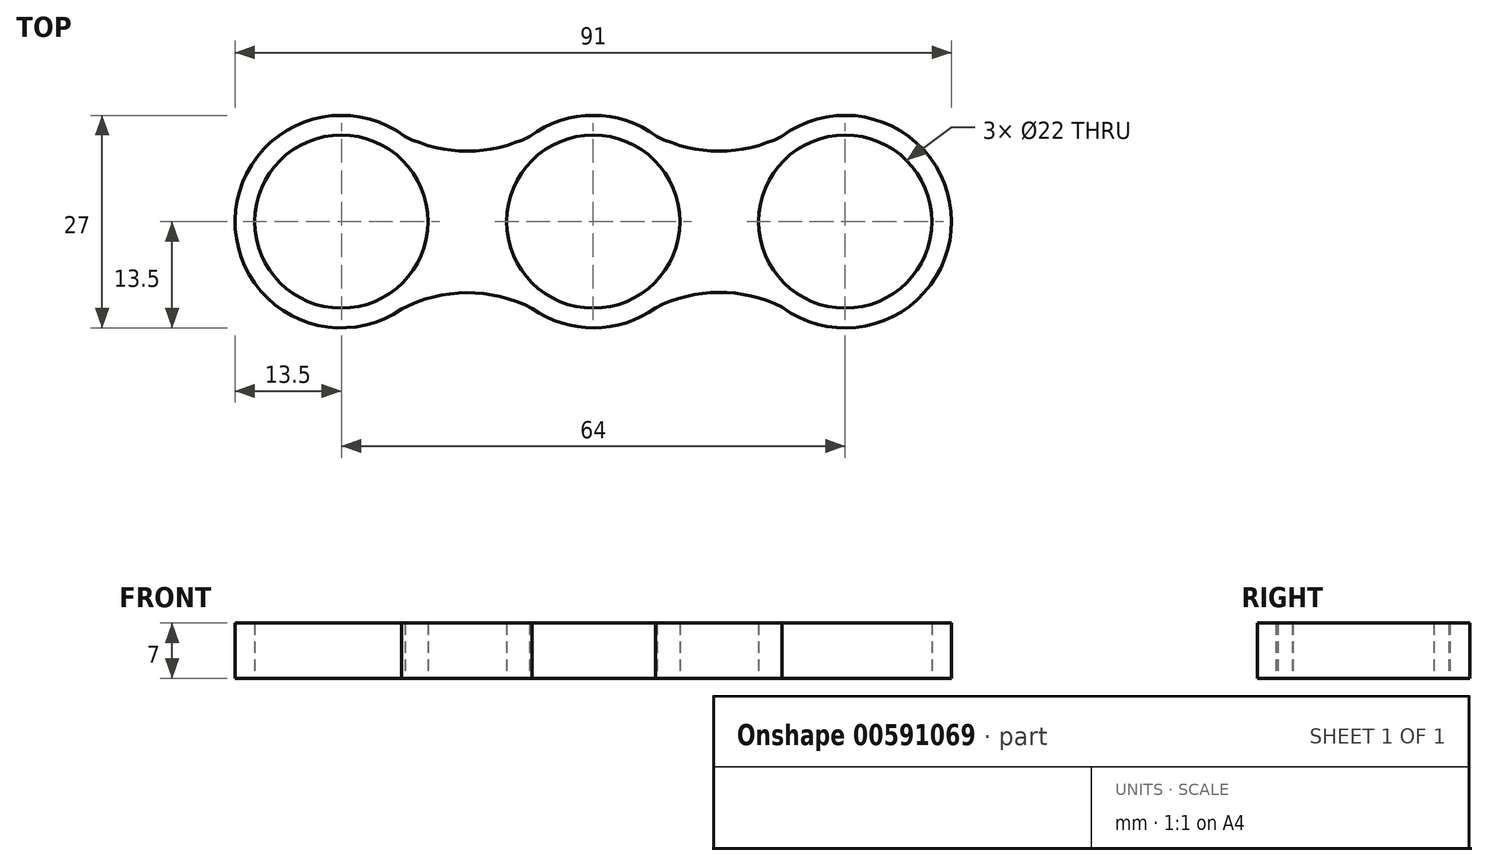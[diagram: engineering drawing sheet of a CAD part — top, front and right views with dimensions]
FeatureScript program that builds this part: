
annotation { "Feature Type Name" : "Feature", "Feature Type Description" : "" }
export const myFeature = defineFeature(function(context is Context, id is Id, definition is map)
    precondition{}
    {
        {
            var Q0;
            Q0=qCreatedBy(makeId("Top.planeOp"),FACE);
            var sketch = newSketch(context, id + "F0", { "sketchPlane" : qUnion([Q0])});
            skCircle(sketch, "E0", {"center": v(-32, 0) * mm, "radius": 11 * mm});
            skCircle(sketch, "E1", {"center": v(-32, 0) * mm, "radius": 13.5 * mm});
            skCircle(sketch, "E2", {"center": v(0, 0) * mm, "radius": 13.5 * mm});
            skCircle(sketch, "E3", {"center": v(0, 0) * mm, "radius": 11 * mm});
            skCircle(sketch, "E4", {"center": v(32, 0) * mm, "radius": 13.5 * mm});
            skCircle(sketch, "E5", {"center": v(32, 0) * mm, "radius": 11 * mm});
            skLineSegment(sketch, "E6", {"start": v(-80.61, -11.44) * mm, "end": v(72.55, -10.6) * mm, "construction": true});
            skLineSegment(sketch, "E7", {"start": v(-81.4, 10.83) * mm, "end": v(77.3, 10.83) * mm, "construction": true});
            skArc(sketch, "E8", {"start": v(-23.94, 10.83) * mm, "mid": v(-16, 8.96) * mm, "end": v(-8.06, 10.83) * mm});
            skArc(sketch, "E9", {"start": v(-7.77, -11.04) * mm, "mid": v(-16.08, -9.03) * mm, "end": v(-24.36, -11.13) * mm});
            skArc(sketch, "E10", {"start": v(24, -10.87) * mm, "mid": v(15.93, -8.98) * mm, "end": v(7.89, -10.96) * mm});
            skArc(sketch, "E11", {"start": v(8.06, 10.83) * mm, "mid": v(16, 8.96) * mm, "end": v(23.94, 10.83) * mm});
            skLineSegment(sketch, "E12", {"start": v(-32, 29.79) * mm, "end": v(-32, -34.2) * mm, "construction": true});
            skLineSegment(sketch, "E13", {"start": v(0, 43.52) * mm, "end": v(0.44, -36.94) * mm, "construction": true});
            skLineSegment(sketch, "E14", {"start": v(32, 40.51) * mm, "end": v(32, -34.49) * mm, "construction": true});
            skSolve(sketch);
        }
        {
            var Q0;
            Q0=qSketchRegion(id+"F0",true);
            extrude(context, id + "F1", {"entities" : qUnion([Q0]), "depth" : 7 * mm});
        }
    });
